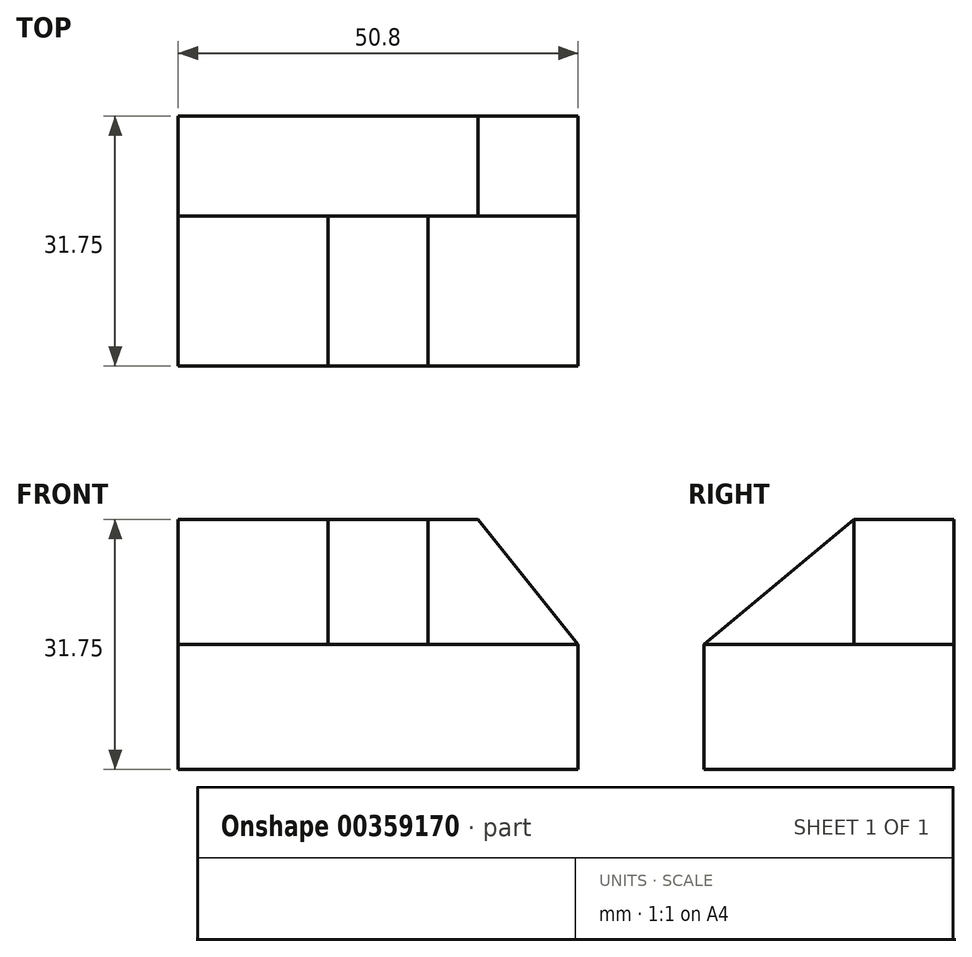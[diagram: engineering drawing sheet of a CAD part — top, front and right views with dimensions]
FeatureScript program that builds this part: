
annotation { "Feature Type Name" : "Feature", "Feature Type Description" : "" }
export const myFeature = defineFeature(function(context is Context, id is Id, definition is map)
    precondition{}
    {
        {
            var Q0;
            Q0=qCreatedBy(makeId("Front.planeOp"),FACE);
            var sketch = newSketch(context, id + "F0", { "sketchPlane" : qUnion([Q0])});
            skLineSegment(sketch, "E0", {"start": v(0, 0) * mm, "end": v(50.8, 0) * mm});
            skLineSegment(sketch, "E1", {"start": v(50.8, 0) * mm, "end": v(50.8, 31.75) * mm});
            skLineSegment(sketch, "E2", {"start": v(50.8, 31.75) * mm, "end": v(0, 31.75) * mm});
            skLineSegment(sketch, "E3", {"start": v(0, 31.75) * mm, "end": v(0, 0) * mm});
            skSolve(sketch);
        }
        {
            var Q0;
            Q0=makeQuery(id+"F0.imprint","IMPRINT",FACE,{"disambiguationData":[TD([[makeQuery(id+"F0.imprint","IMPRINT",EDGE,{"derivedFrom":sQuery(id+"F0.wireOp",EDGE,"E0")}),1.0]])]});
            extrude(context, id + "F1", {"entities" : qUnion([Q0]), "depth" : 31.75 * mm});
        }
        {
            var Q0;
            Q0=makeQuery(id+"F1.opExtrude","CAP_FACE",FACE,{"disambiguationData":[OSD([sQuery(id+"F0.wireOp",EDGE,"E0"),sQuery(id+"F0.wireOp",EDGE,"E1"),sQuery(id+"F0.wireOp",EDGE,"E2"),sQuery(id+"F0.wireOp",EDGE,"E3")])],"isStart":false});
            var sketch = newSketch(context, id + "F2", { "sketchPlane" : qUnion([Q0])});
            skLineSegment(sketch, "E4", {"start": v(38.1, 31.75) * mm, "end": v(50.8, 15.87) * mm});
            skSolve(sketch);
        }
        {
            var Q0;
            {var subQ0=sQuery(id+"F2.wireOp",EDGE,"E4");Q0=makeQuery(id+"F2.imprint","IMPRINT",FACE,{"disambiguationData":[TD([[makeQuery(id+"F2.imprint","IMPRINT",EDGE,{"derivedFrom":subQ0}),1.0]])]});}
            extrude(context, id + "F3", {"entities" : qUnion([Q0]), "operationType" : NewBodyOperationType.REMOVE, "oppositeDirection" : true, "depth" : 12.7 * mm});
        }
        {
            var Q0;
            Q0=makeQuery(id+"F3.boolean.opBoolean","COPY",FACE,{"derivedFrom":makeQuery(id+"F3.opExtrude","CAP_FACE",FACE,{"disambiguationData":[OSD([sQuery(id+"F0.wireOp",EDGE,"E1"),sQuery(id+"F0.wireOp",EDGE,"E2"),sQuery(id+"F2.wireOp",EDGE,"E4")])],"isStart":false})});
            extrude(context, id + "F4", {"entities" : qUnion([Q0]), "operationType" : NewBodyOperationType.REMOVE, "oppositeDirection" : true, "depth" : 19.05 * mm});
        }
        {
            var Q0;
            Q0=makeQuery(id+"F1.opExtrude","CAP_FACE",FACE,{"disambiguationData":[OSD([sQuery(id+"F0.wireOp",EDGE,"E0"),sQuery(id+"F0.wireOp",EDGE,"E1"),sQuery(id+"F0.wireOp",EDGE,"E2"),sQuery(id+"F0.wireOp",EDGE,"E3")])],"isStart":false});
            var sketch = newSketch(context, id + "F5", { "sketchPlane" : qUnion([Q0])});
            skLineSegment(sketch, "E5", {"start": v(31.75, 31.75) * mm, "end": v(31.75, 15.87) * mm});
            skLineSegment(sketch, "E6", {"start": v(31.75, 15.87) * mm, "end": v(50.8, 15.87) * mm});
            skSolve(sketch);
        }
        {
            var Q0;
            {var subQ0=sQuery(id+"F5.wireOp",EDGE,"E5");Q0=makeQuery(id+"F5.imprint","IMPRINT",FACE,{"disambiguationData":[TD([[makeQuery(id+"F5.imprint","IMPRINT",EDGE,{"derivedFrom":subQ0}),1.0]])]});}
            extrude(context, id + "F6", {"entities" : qUnion([Q0]), "operationType" : NewBodyOperationType.REMOVE, "oppositeDirection" : true, "depth" : 19.05 * mm});
        }
        {
            var Q0;
            Q0=makeQuery(id+"F6.boolean.opBoolean","COPY",FACE,{"derivedFrom":makeQuery(id+"F6.opExtrude","SWEPT_FACE",FACE,{"disambiguationData":[OSD([sQuery(id+"F5.wireOp",EDGE,"E5")])]})});
            var sketch = newSketch(context, id + "F7", { "sketchPlane" : qUnion([Q0])});
            skLineSegment(sketch, "E7", {"start": v(-12.7, 31.75) * mm, "end": v(-31.75, 15.87) * mm});
            skSolve(sketch);
        }
        {
            var Q0;
            Q0=makeQuery(id+"F7.imprint","IMPRINT",FACE,{"disambiguationData":[TD([[makeQuery(id+"F7.imprint","IMPRINT",EDGE,{"derivedFrom":sQuery(id+"F7.wireOp",EDGE,"E7")}),-1.0]])]});
            extrude(context, id + "F8", {"entities" : qUnion([Q0]), "operationType" : NewBodyOperationType.REMOVE, "oppositeDirection" : true, "depth" : 31.75 * mm});
        }
        {
            var Q0;
            Q0=makeQuery(id+"F1.opExtrude","SWEPT_FACE",FACE,{"disambiguationData":[OSD([sQuery(id+"F0.wireOp",EDGE,"E3")])]});
            var sketch = newSketch(context, id + "F9", { "sketchPlane" : qUnion([Q0])});
            skLineSegment(sketch, "E8", {"start": v(12.7, 31.75) * mm, "end": v(12.7, 15.88) * mm});
            skPoint(sketch, "E8.endSnap0", {"position": v(0, 15.88) * mm});
            skLineSegment(sketch, "E9", {"start": v(12.7, 15.88) * mm, "end": v(31.75, 15.87) * mm});
            skSolve(sketch);
        }
        {
            var Q0;
            Q0=makeQuery(id+"F9.imprint","IMPRINT",FACE,{"disambiguationData":[TD([[makeQuery(id+"F9.imprint","IMPRINT",EDGE,{"derivedFrom":sQuery(id+"F9.wireOp",EDGE,"E8")}),1.0]])]});
            extrude(context, id + "F10", {"entities" : qUnion([Q0]), "operationType" : NewBodyOperationType.REMOVE, "oppositeDirection" : true, "depth" : 19.05 * mm});
        }
    });
